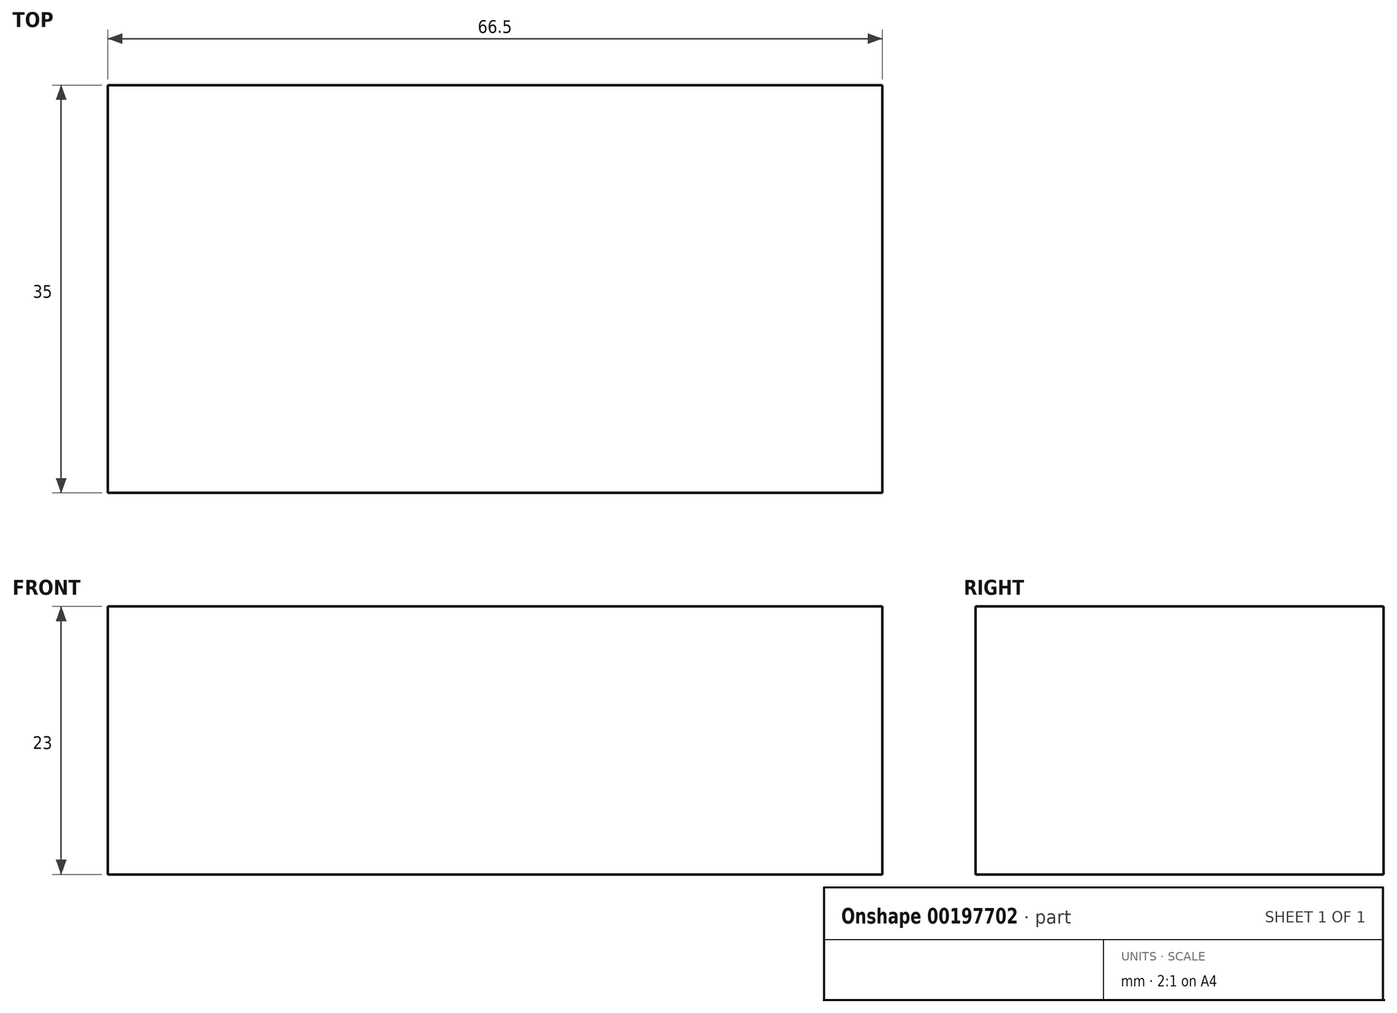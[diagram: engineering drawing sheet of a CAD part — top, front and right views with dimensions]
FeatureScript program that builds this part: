
annotation { "Feature Type Name" : "Feature", "Feature Type Description" : "" }
export const myFeature = defineFeature(function(context is Context, id is Id, definition is map)
    precondition{}
    {
        {
            var Q0;
            Q0=qCreatedBy(makeId("Top.planeOp"),FACE);
            var sketch = newSketch(context, id + "F0", { "sketchPlane" : qUnion([Q0])});
            skLineSegment(sketch, "E0.bottom", {"start": v(33.25, -17.5) * mm, "end": v(-33.25, -17.5) * mm});
            skLineSegment(sketch, "E0.top", {"start": v(33.25, 17.5) * mm, "end": v(-33.25, 17.5) * mm});
            skLineSegment(sketch, "E0.left", {"start": v(33.25, -17.5) * mm, "end": v(33.25, 17.5) * mm});
            skLineSegment(sketch, "E0.right", {"start": v(-33.25, -17.5) * mm, "end": v(-33.25, 17.5) * mm});
            skPoint(sketch, "E0.middle", {"position": v(0, 0) * mm});
            skSolve(sketch);
        }
        {
            var Q0;
            Q0 = qSketchRegion(id + "F0", true);
            extrude(context, id + "F1", {"entities" : qUnion([Q0]), "depth" : 23 * mm});
        }
    });
